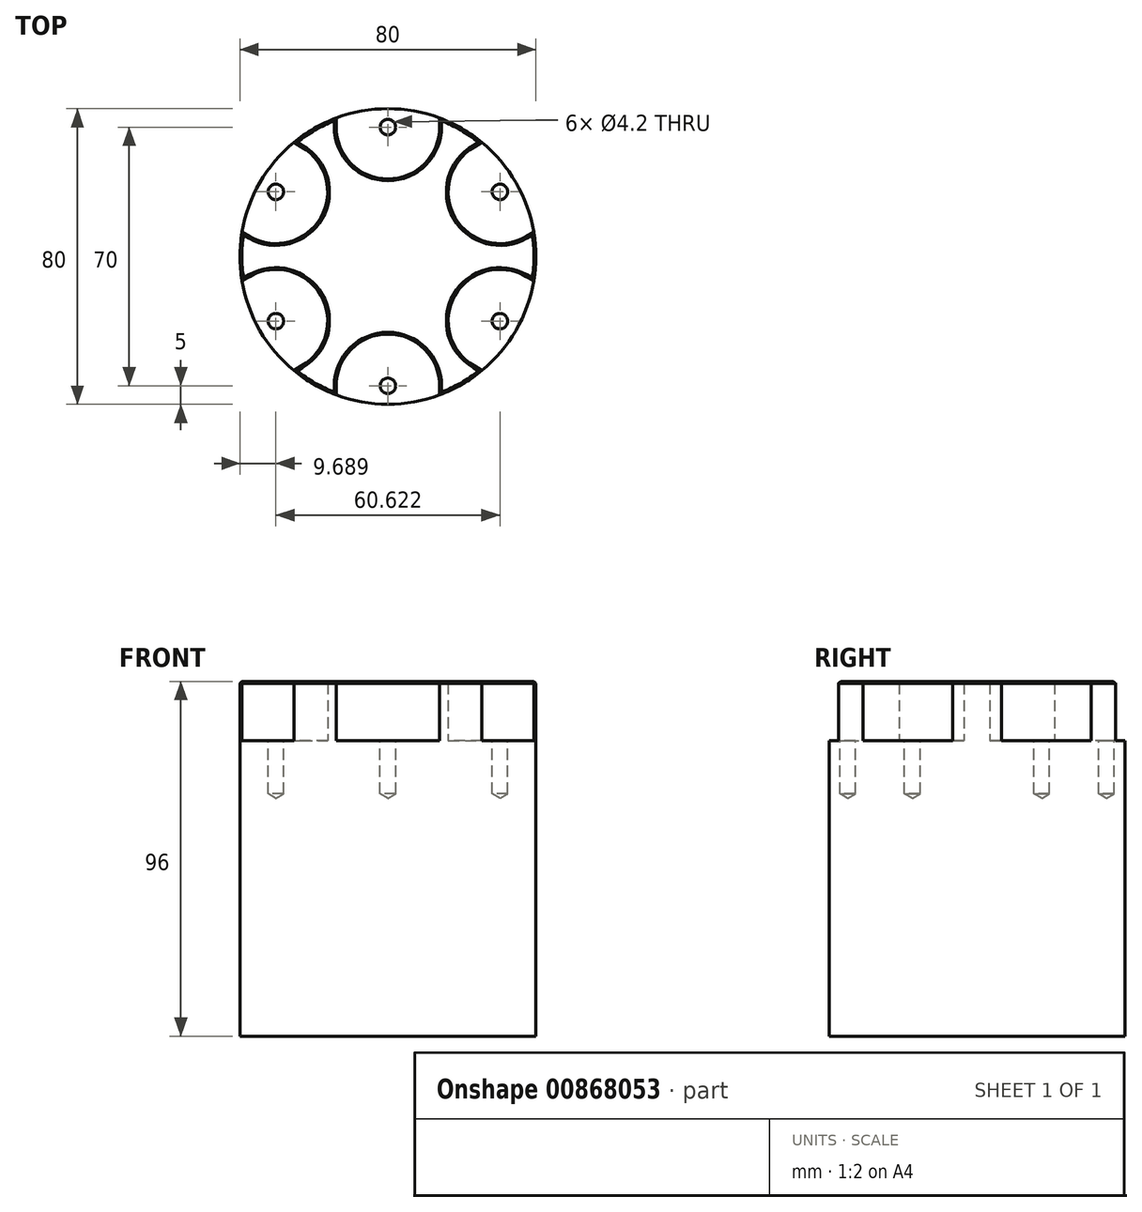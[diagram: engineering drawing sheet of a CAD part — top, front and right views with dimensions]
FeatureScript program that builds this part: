
annotation { "Feature Type Name" : "Feature", "Feature Type Description" : "" }
export const myFeature = defineFeature(function(context is Context, id is Id, definition is map)
    precondition{}
    {
        {
            var Q0;
            Q0=qCreatedBy(makeId("Top.planeOp"),FACE);
            var sketch = newSketch(context, id + "F0", { "sketchPlane" : qUnion([Q0])});
            skCircle(sketch, "E0", {"center": v(0, 0) * mm, "radius": 40 * mm});
            skLineSegment(sketch, "E1", {"start": v(0, 0) * mm, "end": v(0, 40) * mm});
            skLineSegment(sketch, "E2.bottom", {"start": v(14, 37.47) * mm, "end": v(-14, 37.47) * mm});
            skLineSegment(sketch, "E2.top", {"start": v(14, 35) * mm, "end": v(-14, 35) * mm});
            skLineSegment(sketch, "E2.left", {"start": v(14, 37.47) * mm, "end": v(14, 35) * mm});
            skLineSegment(sketch, "E2.right", {"start": v(-14, 37.47) * mm, "end": v(-14, 35) * mm});
            skPoint(sketch, "E2.middle", {"position": v(0, 36.23) * mm});
            skArc(sketch, "E3", {"start": v(-14, 35) * mm, "mid": v(0, 21) * mm, "end": v(14, 35) * mm});
            skPoint(sketch, "E4", {"position": v(0, 20) * mm});
            skArc(sketch, "E5.1.0", {"start": v(-37.31, 5.38) * mm, "mid": v(-18.19, 10.5) * mm, "end": v(-23.31, 29.62) * mm});
            skLineSegment(sketch, "E5.1.1", {"start": v(-25.45, 30.86) * mm, "end": v(-23.31, 29.62) * mm});
            skLineSegment(sketch, "E5.1.2", {"start": v(-39.45, 6.61) * mm, "end": v(-37.31, 5.38) * mm});
            skArc(sketch, "E5.2.0", {"start": v(-23.31, -29.62) * mm, "mid": v(-18.19, -10.5) * mm, "end": v(-37.31, -5.38) * mm});
            skLineSegment(sketch, "E5.2.1", {"start": v(-39.45, -6.61) * mm, "end": v(-37.31, -5.38) * mm});
            skLineSegment(sketch, "E5.2.2", {"start": v(-25.45, -30.86) * mm, "end": v(-23.31, -29.62) * mm});
            skArc(sketch, "E6.2.3.0", {"start": v(14, -35) * mm, "mid": v(0, -21) * mm, "end": v(-14, -35) * mm});
            skLineSegment(sketch, "E6.4.3.0", {"start": v(-14, -37.47) * mm, "end": v(-14, -35) * mm});
            skLineSegment(sketch, "E6.7.3.0", {"start": v(14, -37.47) * mm, "end": v(14, -35) * mm});
            skArc(sketch, "E6.2.4.0", {"start": v(37.31, -5.38) * mm, "mid": v(18.19, -10.5) * mm, "end": v(23.31, -29.62) * mm});
            skLineSegment(sketch, "E6.4.4.0", {"start": v(25.45, -30.86) * mm, "end": v(23.31, -29.62) * mm});
            skLineSegment(sketch, "E6.7.4.0", {"start": v(39.45, -6.61) * mm, "end": v(37.31, -5.38) * mm});
            skArc(sketch, "E6.2.5.0", {"start": v(23.31, 29.62) * mm, "mid": v(18.19, 10.5) * mm, "end": v(37.31, 5.38) * mm});
            skLineSegment(sketch, "E6.4.5.0", {"start": v(39.45, 6.61) * mm, "end": v(37.31, 5.38) * mm});
            skLineSegment(sketch, "E6.7.5.0", {"start": v(25.45, 30.86) * mm, "end": v(23.31, 29.62) * mm});
            skSolve(sketch);
        }
        {
            var Q0;
            {var subQ9=sQuery(id+"F0.wireOp",EDGE,"E2.left");Q0=makeQuery(id+"F0.imprint","IMPRINT",FACE,{"disambiguationData":[TD([[makeQuery(id+"F0.imprint","IMPRINT",EDGE,{"derivedFrom":subQ9}),1.0]])]});}
            var Q1;
            Q1=makeQuery(id+"F0.imprint","IMPRINT",FACE,{"disambiguationData":[TD([[makeQuery(id+"F0.imprint","IMPRINT",EDGE,{"derivedFrom":sQuery(id+"F0.wireOp",EDGE,"E5.1.0")}),1.0]])]});
            var Q2;
            Q2=makeQuery(id+"F0.imprint","IMPRINT",FACE,{"disambiguationData":[TD([[makeQuery(id+"F0.imprint","IMPRINT",EDGE,{"derivedFrom":sQuery(id+"F0.wireOp",EDGE,"E5.2.0")}),1.0]])]});
            var Q3;
            {var subQ0=sQuery(id+"F0.wireOp",EDGE,"E3");var subQ1=sQuery(id+"F0.wireOp",EDGE,"E1");var subQ2=makeQuery(id+"F0.imprint","INTERSECT",VERTEX,{"derivedFrom":[subQ1,subQ0]});Q3=makeQuery(id+"F0.imprint","IMPRINT",FACE,{"disambiguationData":[TD([[makeQuery(id+"F0.imprint","IMPRINT",EDGE,{"disambiguationData":[TD([[subQ2,-1.0]])],"derivedFrom":subQ1}),1.0]])]});}
            var Q4;
            {var subQ0=sQuery(id+"F0.wireOp",EDGE,"E3");var subQ1=sQuery(id+"F0.wireOp",EDGE,"E1");var subQ2=makeQuery(id+"F0.imprint","INTERSECT",VERTEX,{"derivedFrom":[subQ1,subQ0]});Q4=makeQuery(id+"F0.imprint","IMPRINT",FACE,{"disambiguationData":[TD([[makeQuery(id+"F0.imprint","IMPRINT",EDGE,{"disambiguationData":[TD([[subQ2,-1.0]])],"derivedFrom":subQ1}),-1.0]])]});}
            var Q5;
            {var subQ5=sQuery(id+"F0.wireOp",EDGE,"E2.left");Q5=makeQuery(id+"F0.imprint","IMPRINT",FACE,{"disambiguationData":[TD([[makeQuery(id+"F0.imprint","IMPRINT",EDGE,{"derivedFrom":subQ5}),-1.0]])]});}
            var Q6;
            {var subQ0=sQuery(id+"F0.wireOp",EDGE,"E1");var subQ1=sQuery(id+"F0.wireOp",EDGE,"E0");var subQ2=makeQuery(id+"F0.imprint","INTERSECT",VERTEX,{"derivedFrom":[subQ1,subQ0]});Q6=makeQuery(id+"F0.imprint","IMPRINT",FACE,{"disambiguationData":[TD([[makeQuery(id+"F0.imprint","IMPRINT",EDGE,{"disambiguationData":[TD([[subQ2,1.0]])],"derivedFrom":subQ0}),-1.0]])]});}
            var Q7;
            {var subQ0=sQuery(id+"F0.wireOp",EDGE,"E1");var subQ1=sQuery(id+"F0.wireOp",EDGE,"E0");var subQ2=makeQuery(id+"F0.imprint","INTERSECT",VERTEX,{"derivedFrom":[subQ1,subQ0]});Q7=makeQuery(id+"F0.imprint","IMPRINT",FACE,{"disambiguationData":[TD([[makeQuery(id+"F0.imprint","IMPRINT",EDGE,{"disambiguationData":[TD([[subQ2,1.0]])],"derivedFrom":subQ0}),1.0]])]});}
            var Q8;
            {var subQ5=sQuery(id+"F0.wireOp",EDGE,"E2.right");Q8=makeQuery(id+"F0.imprint","IMPRINT",FACE,{"disambiguationData":[TD([[makeQuery(id+"F0.imprint","IMPRINT",EDGE,{"derivedFrom":subQ5}),1.0]])]});}
            var Q9;
            Q9=makeQuery(id+"F0.imprint","IMPRINT",FACE,{"disambiguationData":[TD([[makeQuery(id+"F0.imprint","IMPRINT",EDGE,{"derivedFrom":sQuery(id+"F0.wireOp",EDGE,"E6.2.3.0")}),1.0]])]});
            var Q10;
            Q10=makeQuery(id+"F0.imprint","IMPRINT",FACE,{"disambiguationData":[TD([[makeQuery(id+"F0.imprint","IMPRINT",EDGE,{"derivedFrom":sQuery(id+"F0.wireOp",EDGE,"E6.2.5.0")}),1.0]])]});
            var Q11;
            Q11=makeQuery(id+"F0.imprint","IMPRINT",FACE,{"disambiguationData":[TD([[makeQuery(id+"F0.imprint","IMPRINT",EDGE,{"derivedFrom":sQuery(id+"F0.wireOp",EDGE,"E6.2.4.0")}),1.0]])]});
            extrude(context, id + "F1", {"entities" : qUnion([Q0, Q1, Q2, Q3, Q4, Q5, Q6, Q7, Q8, Q9, Q10, Q11]), "oppositeDirection" : true, "depth" : 80 * mm, "offsetDistance" : 25 * mm, "hasSecondDirection" : true, "secondDirectionOppositeDirection" : false, "secondDirectionDepth" : 16 * mm});
        }
        {
            var Q0;
            Q0=makeQuery(id+"F0.imprint","IMPRINT",FACE,{"disambiguationData":[TD([[makeQuery(id+"F0.imprint","IMPRINT",EDGE,{"derivedFrom":sQuery(id+"F0.wireOp",EDGE,"E5.1.0")}),1.0]])]});
            var Q1;
            Q1=makeQuery(id+"F0.imprint","IMPRINT",FACE,{"disambiguationData":[TD([[makeQuery(id+"F0.imprint","IMPRINT",EDGE,{"derivedFrom":sQuery(id+"F0.wireOp",EDGE,"E5.2.0")}),1.0]])]});
            var Q2;
            {var subQ0=sQuery(id+"F0.wireOp",EDGE,"E3");var subQ1=sQuery(id+"F0.wireOp",EDGE,"E1");var subQ2=makeQuery(id+"F0.imprint","INTERSECT",VERTEX,{"derivedFrom":[subQ1,subQ0]});Q2=makeQuery(id+"F0.imprint","IMPRINT",FACE,{"disambiguationData":[TD([[makeQuery(id+"F0.imprint","IMPRINT",EDGE,{"disambiguationData":[TD([[subQ2,-1.0]])],"derivedFrom":subQ1}),1.0]])]});}
            var Q3;
            {var subQ0=sQuery(id+"F0.wireOp",EDGE,"E1");var subQ1=sQuery(id+"F0.wireOp",EDGE,"E0");var subQ2=makeQuery(id+"F0.imprint","INTERSECT",VERTEX,{"derivedFrom":[subQ1,subQ0]});Q3=makeQuery(id+"F0.imprint","IMPRINT",FACE,{"disambiguationData":[TD([[makeQuery(id+"F0.imprint","IMPRINT",EDGE,{"disambiguationData":[TD([[subQ2,1.0]])],"derivedFrom":subQ0}),1.0]])]});}
            var Q4;
            {var subQ5=sQuery(id+"F0.wireOp",EDGE,"E2.right");Q4=makeQuery(id+"F0.imprint","IMPRINT",FACE,{"disambiguationData":[TD([[makeQuery(id+"F0.imprint","IMPRINT",EDGE,{"derivedFrom":subQ5}),1.0]])]});}
            var Q5;
            {var subQ0=sQuery(id+"F0.wireOp",EDGE,"E1");var subQ1=sQuery(id+"F0.wireOp",EDGE,"E0");var subQ2=makeQuery(id+"F0.imprint","INTERSECT",VERTEX,{"derivedFrom":[subQ1,subQ0]});Q5=makeQuery(id+"F0.imprint","IMPRINT",FACE,{"disambiguationData":[TD([[makeQuery(id+"F0.imprint","IMPRINT",EDGE,{"disambiguationData":[TD([[subQ2,1.0]])],"derivedFrom":subQ0}),-1.0]])]});}
            var Q6;
            {var subQ5=sQuery(id+"F0.wireOp",EDGE,"E2.left");Q6=makeQuery(id+"F0.imprint","IMPRINT",FACE,{"disambiguationData":[TD([[makeQuery(id+"F0.imprint","IMPRINT",EDGE,{"derivedFrom":subQ5}),-1.0]])]});}
            var Q7;
            {var subQ0=sQuery(id+"F0.wireOp",EDGE,"E3");var subQ1=sQuery(id+"F0.wireOp",EDGE,"E1");var subQ2=makeQuery(id+"F0.imprint","INTERSECT",VERTEX,{"derivedFrom":[subQ1,subQ0]});Q7=makeQuery(id+"F0.imprint","IMPRINT",FACE,{"disambiguationData":[TD([[makeQuery(id+"F0.imprint","IMPRINT",EDGE,{"disambiguationData":[TD([[subQ2,-1.0]])],"derivedFrom":subQ1}),-1.0]])]});}
            var Q8;
            Q8=makeQuery(id+"F0.imprint","IMPRINT",FACE,{"disambiguationData":[TD([[makeQuery(id+"F0.imprint","IMPRINT",EDGE,{"derivedFrom":sQuery(id+"F0.wireOp",EDGE,"E6.2.3.0")}),1.0]])]});
            var Q9;
            Q9=makeQuery(id+"F0.imprint","IMPRINT",FACE,{"disambiguationData":[TD([[makeQuery(id+"F0.imprint","IMPRINT",EDGE,{"derivedFrom":sQuery(id+"F0.wireOp",EDGE,"E6.2.5.0")}),1.0]])]});
            var Q10;
            Q10=makeQuery(id+"F0.imprint","IMPRINT",FACE,{"disambiguationData":[TD([[makeQuery(id+"F0.imprint","IMPRINT",EDGE,{"derivedFrom":sQuery(id+"F0.wireOp",EDGE,"E6.2.4.0")}),1.0]])]});
            extrude(context, id + "F2", {"entities" : qUnion([Q0, Q1, Q2, Q3, Q4, Q5, Q6, Q7, Q8, Q9, Q10]), "operationType" : NewBodyOperationType.REMOVE, "depth" : 25 * mm, "offsetDistance" : 25 * mm});
        }
        {
            var Q0;
            Q0=sQuery(id+"F0.wireOp",VERTEX,"E5.1.0.center");
            var Q1;
            Q1=sQuery(id+"F0.wireOp",VERTEX,"E5.2.0.center");
            var Q2;
            Q2=sQuery(id+"F0.wireOp",VERTEX,"E3.center");
            var Q3;
            Q3=sQuery(id+"F0.wireOp",VERTEX,"E6.2.5.0.center");
            var Q4;
            Q4=sQuery(id+"F0.wireOp",VERTEX,"E6.2.4.0.center");
            var Q5;
            Q5=sQuery(id+"F0.wireOp",VERTEX,"E6.2.3.0.center");
            var Q6;
            Q6=makeQuery(id+"F1.opExtrude","SWEPT_BODY",BODY,{"disambiguationData":[OSD([sQuery(id+"F0.wireOp",EDGE,"E0")])]});
            hole(context, id + "F3", {"style" : HoleStyle.SIMPLE, "endStyle" : HoleEndStyle.BLIND, "standardTappedOrClearance" : lookupTablePath({ "standard" : "ISO", "engagement" : "75%", "pitch" : "0.8 mm", "size" : "M5", "type" : "Tapped" }), "standardBlindInLast" : lookupTablePath({ "standard" : "ISO", "engagement" : "75%", "pitch" : "0.8 mm", "size" : "M5", "type" : "Tapped" }), "holeDiameter" : 4.2 * mm, "majorDiameter" : 5 * mm, "showTappedDepth" : true, "holeDepth" : 14.4 * mm, "tappedDepth" : 12 * mm, "tapClearance" : 3, "startFromSketch" : true, "locations" : qUnion([Q0, Q1, Q2, Q3, Q4, Q5]), "scope" : qUnion([Q6])});
        }
        {
            var Q0;
            Q0=makeQuery(id+"F2.boolean.opBoolean","INTERSECT",EDGE,{"derivedFrom":[makeQuery(id+"F1.opExtrude","CAP_FACE",FACE,{"disambiguationData":[OSD([sQuery(id+"F0.wireOp",EDGE,"E0")])],"isStart":true}),makeQuery(id+"F2.opExtrude","SWEPT_FACE",FACE,{"disambiguationData":[OSD([sQuery(id+"F0.wireOp",EDGE,"E3")])]})]});
            var Q1;
            Q1=makeQuery(id+"F2.boolean.opBoolean","INTERSECT",EDGE,{"derivedFrom":[makeQuery(id+"F1.opExtrude","CAP_FACE",FACE,{"disambiguationData":[OSD([sQuery(id+"F0.wireOp",EDGE,"E0")])],"isStart":true}),makeQuery(id+"F2.opExtrude","SWEPT_FACE",FACE,{"disambiguationData":[OSD([sQuery(id+"F0.wireOp",EDGE,"E5.1.0")])]})]});
            var Q2;
            Q2=makeQuery(id+"F2.boolean.opBoolean","INTERSECT",EDGE,{"derivedFrom":[makeQuery(id+"F1.opExtrude","CAP_FACE",FACE,{"disambiguationData":[OSD([sQuery(id+"F0.wireOp",EDGE,"E0")])],"isStart":true}),makeQuery(id+"F2.opExtrude","SWEPT_FACE",FACE,{"disambiguationData":[OSD([sQuery(id+"F0.wireOp",EDGE,"E5.2.0")])]})]});
            var Q3;
            Q3=makeQuery(id+"F2.boolean.opBoolean","INTERSECT",EDGE,{"derivedFrom":[makeQuery(id+"F1.opExtrude","CAP_FACE",FACE,{"disambiguationData":[OSD([sQuery(id+"F0.wireOp",EDGE,"E0")])],"isStart":true}),makeQuery(id+"F2.opExtrude","SWEPT_FACE",FACE,{"disambiguationData":[OSD([sQuery(id+"F0.wireOp",EDGE,"E6.2.3.0")])]})]});
            var Q4;
            Q4=makeQuery(id+"F2.boolean.opBoolean","INTERSECT",EDGE,{"derivedFrom":[makeQuery(id+"F1.opExtrude","CAP_FACE",FACE,{"disambiguationData":[OSD([sQuery(id+"F0.wireOp",EDGE,"E0")])],"isStart":true}),makeQuery(id+"F2.opExtrude","SWEPT_FACE",FACE,{"disambiguationData":[OSD([sQuery(id+"F0.wireOp",EDGE,"E6.2.4.0")])]})]});
            var Q5;
            Q5=makeQuery(id+"F2.boolean.opBoolean","INTERSECT",EDGE,{"derivedFrom":[makeQuery(id+"F1.opExtrude","CAP_FACE",FACE,{"disambiguationData":[OSD([sQuery(id+"F0.wireOp",EDGE,"E0")])],"isStart":true}),makeQuery(id+"F2.opExtrude","SWEPT_FACE",FACE,{"disambiguationData":[OSD([sQuery(id+"F0.wireOp",EDGE,"E6.2.5.0")])]})]});
            var Q6;
            {var subQ0=sQuery(id+"F0.wireOp",EDGE,"E0");var subQ1=makeQuery(id+"F0.imprint","INTERSECT",VERTEX,{"derivedFrom":[subQ0,sQuery(id+"F0.wireOp",EDGE,"E1")]});Q6=makeQuery(id+"F2.boolean.opBoolean","COPY",EDGE,{"derivedFrom":makeQuery(id+"F2.opExtrude","CAP_EDGE",EDGE,{"disambiguationData":[OSD([subQ0]),TDD([makeQuery(id+"F0.imprint","IMPRINT",EDGE,{"disambiguationData":[TD([[subQ1,1.0]])],"derivedFrom":subQ0}),makeQuery(id+"F0.imprint","IMPRINT",EDGE,{"disambiguationData":[TD([[subQ1,-1.0]])],"derivedFrom":subQ0})])],"isStart":true})});}
            var Q7;
            {var subQ0=sQuery(id+"F0.wireOp",EDGE,"E0");Q7=makeQuery(id+"F2.boolean.opBoolean","COPY",EDGE,{"derivedFrom":makeQuery(id+"F2.opExtrude","CAP_EDGE",EDGE,{"disambiguationData":[OSD([subQ0]),TDD([makeQuery(id+"F0.imprint","IMPRINT",EDGE,{"disambiguationData":[TD([[makeQuery(id+"F0.imprint","INTERSECT",VERTEX,{"derivedFrom":[subQ0,sQuery(id+"F0.wireOp",EDGE,"E5.1.1")]}),-1.0]])],"derivedFrom":subQ0})])],"isStart":true})});}
            var Q8;
            {var subQ0=sQuery(id+"F0.wireOp",EDGE,"E0");Q8=makeQuery(id+"F2.boolean.opBoolean","COPY",EDGE,{"derivedFrom":makeQuery(id+"F2.opExtrude","CAP_EDGE",EDGE,{"disambiguationData":[OSD([subQ0]),TDD([makeQuery(id+"F0.imprint","IMPRINT",EDGE,{"disambiguationData":[TD([[makeQuery(id+"F0.imprint","INTERSECT",VERTEX,{"derivedFrom":[subQ0,sQuery(id+"F0.wireOp",EDGE,"E5.2.1")]}),-1.0]])],"derivedFrom":subQ0})])],"isStart":true})});}
            var Q9;
            {var subQ0=sQuery(id+"F0.wireOp",EDGE,"E0");Q9=makeQuery(id+"F2.boolean.opBoolean","COPY",EDGE,{"derivedFrom":makeQuery(id+"F2.opExtrude","CAP_EDGE",EDGE,{"disambiguationData":[OSD([subQ0]),TDD([makeQuery(id+"F0.imprint","IMPRINT",EDGE,{"disambiguationData":[TD([[makeQuery(id+"F0.imprint","INTERSECT",VERTEX,{"derivedFrom":[subQ0,sQuery(id+"F0.wireOp",EDGE,"E6.4.5.0")]}),-1.0]])],"derivedFrom":subQ0})])],"isStart":true})});}
            var Q10;
            {var subQ0=sQuery(id+"F0.wireOp",EDGE,"E0");Q10=makeQuery(id+"F2.boolean.opBoolean","COPY",EDGE,{"derivedFrom":makeQuery(id+"F2.opExtrude","CAP_EDGE",EDGE,{"disambiguationData":[OSD([subQ0]),TDD([makeQuery(id+"F0.imprint","IMPRINT",EDGE,{"disambiguationData":[TD([[makeQuery(id+"F0.imprint","INTERSECT",VERTEX,{"derivedFrom":[subQ0,sQuery(id+"F0.wireOp",EDGE,"E6.4.4.0")]}),-1.0]])],"derivedFrom":subQ0})])],"isStart":true})});}
            var Q11;
            {var subQ0=sQuery(id+"F0.wireOp",EDGE,"E0");Q11=makeQuery(id+"F2.boolean.opBoolean","COPY",EDGE,{"derivedFrom":makeQuery(id+"F2.opExtrude","CAP_EDGE",EDGE,{"disambiguationData":[OSD([subQ0]),TDD([makeQuery(id+"F0.imprint","IMPRINT",EDGE,{"disambiguationData":[TD([[makeQuery(id+"F0.imprint","INTERSECT",VERTEX,{"derivedFrom":[subQ0,sQuery(id+"F0.wireOp",EDGE,"E6.4.3.0")]}),-1.0]])],"derivedFrom":subQ0})])],"isStart":true})});}
            var Q12;
            Q12=makeQuery(id+"F2.boolean.opBoolean","COPY",EDGE,{"derivedFrom":makeQuery(id+"F2.opExtrude","SWEPT_EDGE",EDGE,{"disambiguationData":[OSD([sQuery(id+"F0.wireOp",EDGE,"E0"),sQuery(id+"F0.wireOp",EDGE,"E2.bottom"),sQuery(id+"F0.wireOp",EDGE,"E2.left")])]})});
            var Q13;
            Q13=makeQuery(id+"F2.boolean.opBoolean","COPY",EDGE,{"derivedFrom":makeQuery(id+"F2.opExtrude","SWEPT_EDGE",EDGE,{"disambiguationData":[OSD([sQuery(id+"F0.wireOp",EDGE,"E0"),sQuery(id+"F0.wireOp",EDGE,"E2.bottom"),sQuery(id+"F0.wireOp",EDGE,"E2.right")])]})});
            var Q14;
            Q14=makeQuery(id+"F2.boolean.opBoolean","COPY",EDGE,{"derivedFrom":makeQuery(id+"F2.opExtrude","SWEPT_EDGE",EDGE,{"disambiguationData":[OSD([sQuery(id+"F0.wireOp",EDGE,"E0"),sQuery(id+"F0.wireOp",EDGE,"E5.1.1")])]})});
            var Q15;
            Q15=makeQuery(id+"F2.boolean.opBoolean","COPY",EDGE,{"derivedFrom":makeQuery(id+"F2.opExtrude","SWEPT_EDGE",EDGE,{"disambiguationData":[OSD([sQuery(id+"F0.wireOp",EDGE,"E0"),sQuery(id+"F0.wireOp",EDGE,"E5.1.2")])]})});
            var Q16;
            Q16=makeQuery(id+"F2.boolean.opBoolean","COPY",EDGE,{"derivedFrom":makeQuery(id+"F2.opExtrude","SWEPT_EDGE",EDGE,{"disambiguationData":[OSD([sQuery(id+"F0.wireOp",EDGE,"E0"),sQuery(id+"F0.wireOp",EDGE,"E5.2.1")])]})});
            var Q17;
            Q17=makeQuery(id+"F2.boolean.opBoolean","COPY",EDGE,{"derivedFrom":makeQuery(id+"F2.opExtrude","SWEPT_EDGE",EDGE,{"disambiguationData":[OSD([sQuery(id+"F0.wireOp",EDGE,"E0"),sQuery(id+"F0.wireOp",EDGE,"E5.2.2")])]})});
            var Q18;
            Q18=makeQuery(id+"F2.boolean.opBoolean","COPY",EDGE,{"derivedFrom":makeQuery(id+"F2.opExtrude","SWEPT_EDGE",EDGE,{"disambiguationData":[OSD([sQuery(id+"F0.wireOp",EDGE,"E0"),sQuery(id+"F0.wireOp",EDGE,"E6.7.3.0")])]})});
            var Q19;
            Q19=makeQuery(id+"F2.boolean.opBoolean","COPY",EDGE,{"derivedFrom":makeQuery(id+"F2.opExtrude","SWEPT_EDGE",EDGE,{"disambiguationData":[OSD([sQuery(id+"F0.wireOp",EDGE,"E0"),sQuery(id+"F0.wireOp",EDGE,"E6.7.4.0")])]})});
            var Q20;
            Q20=makeQuery(id+"F2.boolean.opBoolean","COPY",EDGE,{"derivedFrom":makeQuery(id+"F2.opExtrude","SWEPT_EDGE",EDGE,{"disambiguationData":[OSD([sQuery(id+"F0.wireOp",EDGE,"E0"),sQuery(id+"F0.wireOp",EDGE,"E6.4.5.0")])]})});
            var Q21;
            Q21=makeQuery(id+"F2.boolean.opBoolean","COPY",EDGE,{"derivedFrom":makeQuery(id+"F2.opExtrude","SWEPT_EDGE",EDGE,{"disambiguationData":[OSD([sQuery(id+"F0.wireOp",EDGE,"E0"),sQuery(id+"F0.wireOp",EDGE,"E6.4.3.0")])]})});
            var Q22;
            Q22=makeQuery(id+"F2.boolean.opBoolean","COPY",EDGE,{"derivedFrom":makeQuery(id+"F2.opExtrude","SWEPT_EDGE",EDGE,{"disambiguationData":[OSD([sQuery(id+"F0.wireOp",EDGE,"E0"),sQuery(id+"F0.wireOp",EDGE,"E6.4.4.0")])]})});
            var Q23;
            Q23=makeQuery(id+"F2.boolean.opBoolean","COPY",EDGE,{"derivedFrom":makeQuery(id+"F2.opExtrude","SWEPT_EDGE",EDGE,{"disambiguationData":[OSD([sQuery(id+"F0.wireOp",EDGE,"E0"),sQuery(id+"F0.wireOp",EDGE,"E6.7.5.0")])]})});
            var Q24;
            {var subQ0=sQuery(id+"F0.wireOp",EDGE,"E0");Q24=makeQuery(id+"F2.boolean.opBoolean","SPLIT",EDGE,{"disambiguationData":[TD([makeQuery(id+"F2.opExtrude","SWEPT_FACE",FACE,{"disambiguationData":[OSD([sQuery(id+"F0.wireOp",EDGE,"E6.7.4.0")])]})])],"derivedFrom":makeQuery(id+"F1.opExtrude","CAP_EDGE",EDGE,{"disambiguationData":[OSD([subQ0])],"isStart":true})});}
            var Q25;
            {var subQ0=sQuery(id+"F0.wireOp",EDGE,"E0");Q25=makeQuery(id+"F2.boolean.opBoolean","SPLIT",EDGE,{"disambiguationData":[TD([makeQuery(id+"F2.opExtrude","SWEPT_FACE",FACE,{"disambiguationData":[OSD([sQuery(id+"F0.wireOp",EDGE,"E2.left")])]})])],"derivedFrom":makeQuery(id+"F1.opExtrude","CAP_EDGE",EDGE,{"disambiguationData":[OSD([subQ0])],"isStart":true})});}
            var Q26;
            {var subQ0=sQuery(id+"F0.wireOp",EDGE,"E0");Q26=makeQuery(id+"F2.boolean.opBoolean","SPLIT",EDGE,{"disambiguationData":[TD([makeQuery(id+"F2.opExtrude","SWEPT_FACE",FACE,{"disambiguationData":[OSD([sQuery(id+"F0.wireOp",EDGE,"E6.7.3.0")])]})])],"derivedFrom":makeQuery(id+"F1.opExtrude","CAP_EDGE",EDGE,{"disambiguationData":[OSD([subQ0])],"isStart":true})});}
            var Q27;
            {var subQ0=sQuery(id+"F0.wireOp",EDGE,"E0");Q27=makeQuery(id+"F2.boolean.opBoolean","SPLIT",EDGE,{"disambiguationData":[TD([makeQuery(id+"F2.opExtrude","SWEPT_FACE",FACE,{"disambiguationData":[OSD([sQuery(id+"F0.wireOp",EDGE,"E5.2.2")])]})])],"derivedFrom":makeQuery(id+"F1.opExtrude","CAP_EDGE",EDGE,{"disambiguationData":[OSD([subQ0])],"isStart":true})});}
            var Q28;
            {var subQ0=sQuery(id+"F0.wireOp",EDGE,"E0");Q28=makeQuery(id+"F2.boolean.opBoolean","SPLIT",EDGE,{"disambiguationData":[TD([makeQuery(id+"F2.opExtrude","SWEPT_FACE",FACE,{"disambiguationData":[OSD([sQuery(id+"F0.wireOp",EDGE,"E5.1.2")])]})])],"derivedFrom":makeQuery(id+"F1.opExtrude","CAP_EDGE",EDGE,{"disambiguationData":[OSD([subQ0])],"isStart":true})});}
            var Q29;
            {var subQ0=sQuery(id+"F0.wireOp",EDGE,"E0");Q29=makeQuery(id+"F2.boolean.opBoolean","SPLIT",EDGE,{"disambiguationData":[TD([makeQuery(id+"F2.opExtrude","SWEPT_FACE",FACE,{"disambiguationData":[OSD([sQuery(id+"F0.wireOp",EDGE,"E2.right")])]})])],"derivedFrom":makeQuery(id+"F1.opExtrude","CAP_EDGE",EDGE,{"disambiguationData":[OSD([subQ0])],"isStart":true})});}
            chamfer(context, id + "F4", {"entities" : qUnion([Q0, Q1, Q2, Q3, Q4, Q5, Q6, Q7, Q8, Q9, Q10, Q11, Q12, Q13, Q14, Q15, Q16, Q17, Q18, Q19, Q20, Q21, Q22, Q23, Q24, Q25, Q26, Q27, Q28, Q29]), "width" : .5 * mm, "tangentPropagation" : true});
        }
    });
